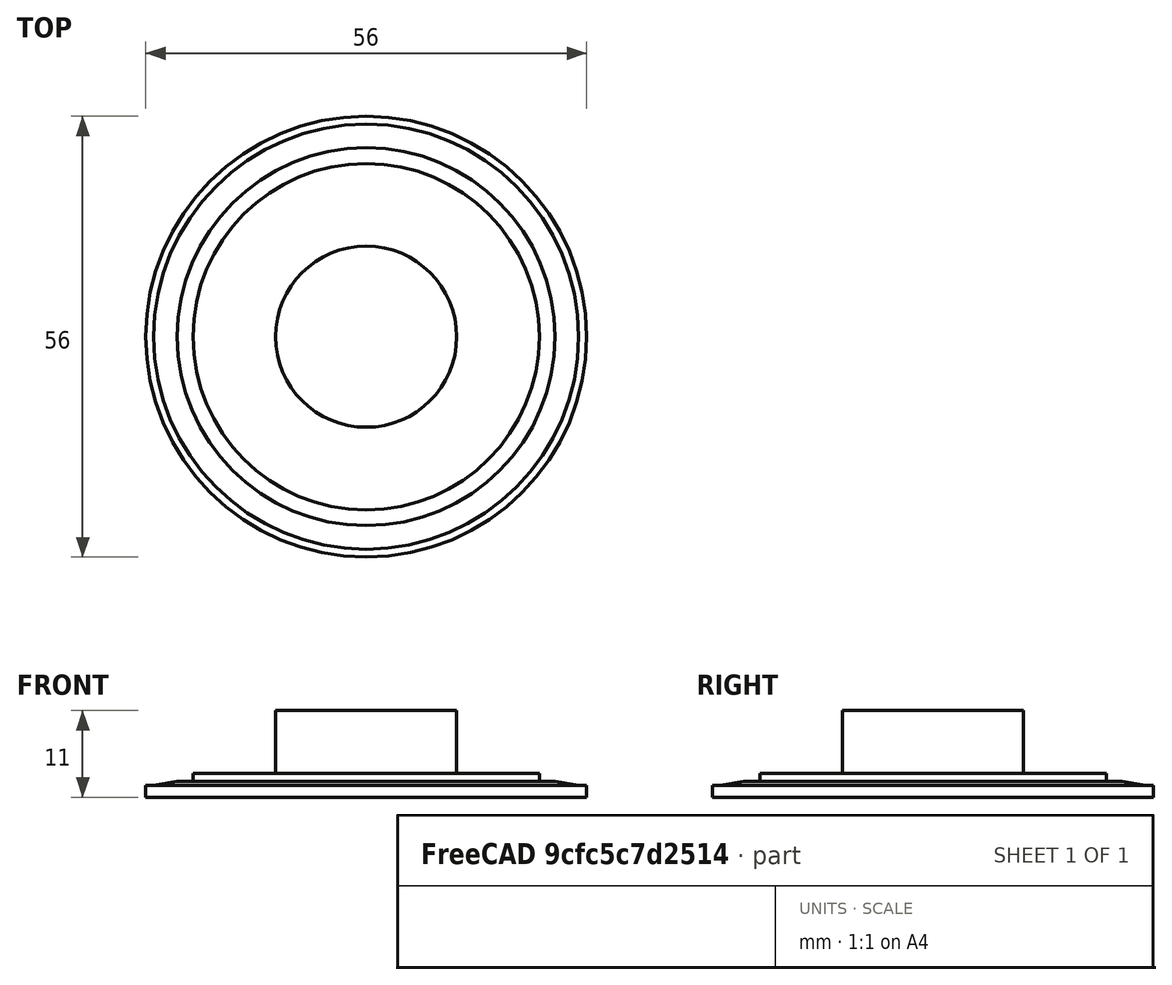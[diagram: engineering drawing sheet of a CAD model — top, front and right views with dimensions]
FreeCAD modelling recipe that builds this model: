
FCSTD DOCUMENT  (FreeCAD 0.20R29410 (Git))
Label: _Speaker
License: Creative Commons Attribution
LicenseURL: http://creativecommons.org/licenses/by/4.0/
objects: Sketcher::SketchObject×1, PartDesign::Revolution×1, PartDesign::Body×1, Part::Feature×1
note: 5 computed .brp shape members not serialized (recipe doc carries the construction recipe); baked Part::Feature solids carry a one-line shape summary decoded from their .brp

FEATURE [Sketcher::SketchObject] Sketch
  FullyConstrained = true
  MapMode = 5
  Placement = pos=(0,0,0) rot=(1,0,0;1.5708rad)
  Support = -> [XZ_Plane]
  sketch-geometry (10):
    g0: LineSegment StartX=0 StartY=0 StartZ=0 EndX=28 EndY=0 EndZ=0
    g1: LineSegment StartX=28 StartY=0 StartZ=0 EndX=28 EndY=1.5 EndZ=0
    g2: LineSegment StartX=28 StartY=1.5 StartZ=0 EndX=27 EndY=1.5 EndZ=0
    g3: LineSegment StartX=27 StartY=1.5 StartZ=0 EndX=24 EndY=2 EndZ=0
    g4: LineSegment StartX=24 StartY=2 StartZ=0 EndX=22 EndY=2 EndZ=0
    g5: LineSegment StartX=22 StartY=2 StartZ=0 EndX=22 EndY=3 EndZ=0
    g6: LineSegment StartX=22 StartY=3 StartZ=0 EndX=11.5 EndY=3 EndZ=0
    g7: LineSegment StartX=11.5 StartY=3 StartZ=0 EndX=11.5 EndY=11 EndZ=0
    g8: LineSegment StartX=11.5 StartY=11 StartZ=0 EndX=0 EndY=11 EndZ=0
    g9: LineSegment StartX=0 StartY=11 StartZ=0 EndX=0 EndY=0 EndZ=0
  constraints (29):
    c: Coincident(g-1,g0)
    c: Horizontal(g0)
    c: Coincident(g0,g1)
    c: Vertical(g1)
    c: Coincident(g1,g2)
    c: Horizontal(g2)
    c: Coincident(g2,g3)
    c: Coincident(g3,g4)
    c: Coincident(g4,g5)
    c: Vertical(g5)
    c: Coincident(g5,g6)
    c: Horizontal(g6)
    c: Coincident(g6,g7)
    c: Vertical(g7)
    c: Coincident(g7,g8)
    c: Horizontal(g8)
    c: Coincident(g8,g9)
    c: Coincident(g9,g0)
    c: Vertical(g9)
    c: DistanceX(g0,g0) = 28
    c: DistanceY(g9,g9) = 11
    c: DistanceX(g8,g8) = 11.5
    c: DistanceX(g2,g2) = 1
    c: Horizontal(g4)
    c: DistanceX(g8,g5) = 22
    c: DistanceX(g4,g4) = 2
    c: DistanceY(g0,g5) = 3
    c: DistanceY(g5,g5) = 1
    c: DistanceY(g1,g1) = 1.5
FEATURE [PartDesign::Revolution] Revolution
  Angle = 360
  Axis = (0,2e-16,1)
  Base = (0,0,0)
  Placement = pos=(0,0,0) rot=(1,0,0;1.5708rad)
  Profile = -> Sketch
  ReferenceAxis = -> Sketch [V_Axis]
  Reversed = true
FEATURE [PartDesign::Body] Body
  Group = -> [Sketch,Revolution]
  Origin = -> Origin
  Tip = -> Revolution
FEATURE [Part::Feature] Body001  label="Speaker"
  shape: bbox 56 x 56 x 11 mm, 9 faces (baked)
